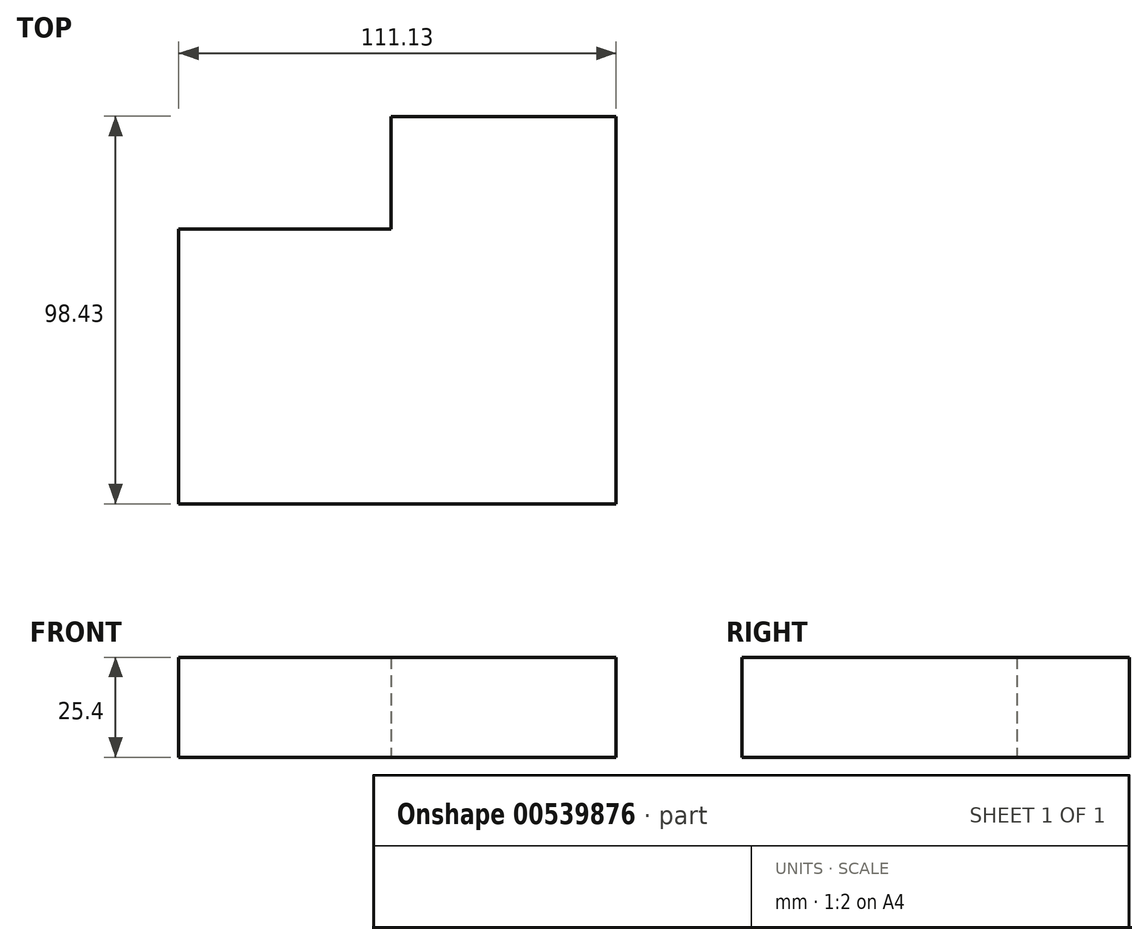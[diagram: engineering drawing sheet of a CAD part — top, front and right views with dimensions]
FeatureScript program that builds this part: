
annotation { "Feature Type Name" : "Feature", "Feature Type Description" : "" }
export const myFeature = defineFeature(function(context is Context, id is Id, definition is map)
    precondition{}
    {
        {
            var Q0;
            Q0=qCreatedBy(makeId("Top.planeOp"),FACE);
            var sketch = newSketch(context, id + "F0", { "sketchPlane" : qUnion([Q0])});
            skLineSegment(sketch, "E0", {"start": v(-59.88, -36.65) * mm, "end": v(51.25, -36.65) * mm});
            skLineSegment(sketch, "E1", {"start": v(51.25, -36.65) * mm, "end": v(51.25, 61.78) * mm});
            skLineSegment(sketch, "E2", {"start": v(51.25, 61.78) * mm, "end": v(-5.9, 61.78) * mm});
            skLineSegment(sketch, "E3", {"start": v(-59.88, -36.65) * mm, "end": v(-59.88, 33.2) * mm});
            skLineSegment(sketch, "E4", {"start": v(-59.88, 33.2) * mm, "end": v(-5.9, 33.2) * mm});
            skLineSegment(sketch, "E5", {"start": v(-5.9, 33.2) * mm, "end": v(-5.9, 61.78) * mm});
            skSolve(sketch);
        }
        {
            var Q0;
            Q0 = qSketchRegion(id + "F0", true);
            extrude(context, id + "F1", {"entities" : qUnion([Q0]), "depth" : 25.4 * mm, "offsetDistance" : 25.4 * mm});
        }
    });
